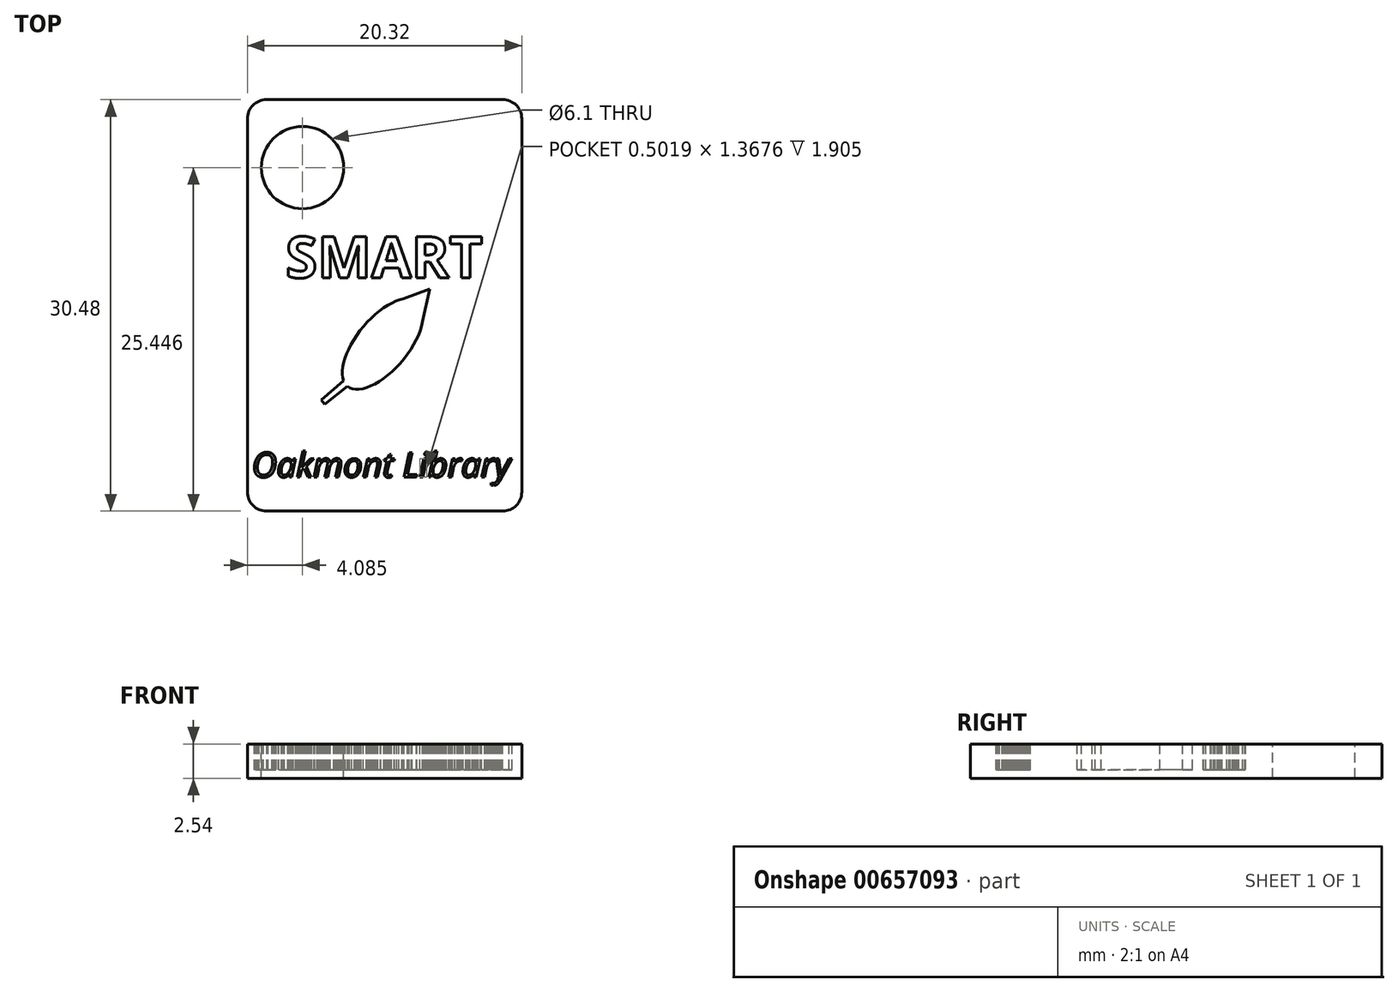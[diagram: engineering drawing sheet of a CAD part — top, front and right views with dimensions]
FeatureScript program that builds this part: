
annotation { "Feature Type Name" : "Feature", "Feature Type Description" : "" }
export const myFeature = defineFeature(function(context is Context, id is Id, definition is map)
    precondition{}
    {
        {
            var Q0;
            Q0=qCreatedBy(makeId("Top.planeOp"),FACE);
            var sketch = newSketch(context, id + "F0", { "sketchPlane" : qUnion([Q0])});
            skLineSegment(sketch, "E0.bottom", {"start": v(10.16, -15.24) * mm, "end": v(-10.16, -15.24) * mm});
            skLineSegment(sketch, "E0.top", {"start": v(10.16, 15.24) * mm, "end": v(-10.16, 15.24) * mm});
            skLineSegment(sketch, "E0.left", {"start": v(10.16, -15.24) * mm, "end": v(10.16, 15.24) * mm});
            skLineSegment(sketch, "E0.right", {"start": v(-10.16, -15.24) * mm, "end": v(-10.16, 15.24) * mm});
            skPoint(sketch, "E0.middle", {"position": v(0, 0) * mm});
            skSolve(sketch);
        }
        {
            var Q0;
            Q0 = qSketchRegion(id + "F0", true);
            extrude(context, id + "F1", {"entities" : qUnion([Q0]), "depth" : 2.54 * mm, "offsetDistance" : 25.4 * mm});
        }
        {
            var Q0;
            Q0=makeQuery(id+"F1.opExtrude","CAP_FACE",FACE,{"disambiguationData":[OSD([sQuery(id+"F0.wireOp",EDGE,"E0.bottom"),sQuery(id+"F0.wireOp",EDGE,"E0.top"),sQuery(id+"F0.wireOp",EDGE,"E0.left"),sQuery(id+"F0.wireOp",EDGE,"E0.right")])],"isStart":false});
            var sketch = newSketch(context, id + "F2", { "sketchPlane" : qUnion([Q0])});
            skText(sketch, "E1", { "text": "SMART\n", "fontName": "OpenSans-Bold.ttf"});
            const initialGuessF2  = {"E1": [-0.00734, 0.00204, 1, 0, 0.00307]};
            skSetInitialGuess(sketch, initialGuessF2);
            skSolve(sketch);
        }
        {
            var Q0;
            Q0 = qSketchRegion(id + "F2", true);
            extrude(context, id + "F3", {"entities" : qUnion([Q0]), "operationType" : NewBodyOperationType.REMOVE, "oppositeDirection" : true, "depth" : 1.9 * mm, "offsetDistance" : 25.4 * mm});
        }
        {
            var Q0;
            Q0=makeQuery(id+"F1.opExtrude","SWEPT_EDGE",EDGE,{"disambiguationData":[OSD([sQuery(id+"F0.wireOp",EDGE,"E0.top"),sQuery(id+"F0.wireOp",EDGE,"E0.right")])]});
            var Q1;
            Q1=makeQuery(id+"F1.opExtrude","SWEPT_EDGE",EDGE,{"disambiguationData":[OSD([sQuery(id+"F0.wireOp",EDGE,"E0.top"),sQuery(id+"F0.wireOp",EDGE,"E0.left")])]});
            var Q2;
            Q2=makeQuery(id+"F1.opExtrude","SWEPT_EDGE",EDGE,{"disambiguationData":[OSD([sQuery(id+"F0.wireOp",EDGE,"E0.bottom"),sQuery(id+"F0.wireOp",EDGE,"E0.left")])]});
            var Q3;
            Q3=makeQuery(id+"F1.opExtrude","SWEPT_EDGE",EDGE,{"disambiguationData":[OSD([sQuery(id+"F0.wireOp",EDGE,"E0.bottom"),sQuery(id+"F0.wireOp",EDGE,"E0.right")])]});
            fillet(context, id + "F4", {"entities" : qUnion([Q0, Q1, Q2, Q3]), "radius" : 1.41 * mm, "tangentPropagation" : true, "allowEdgeOverflow" : false});
        }
        {
            var Q0;
            {var subQ0=sQuery(id+"F0.wireOp",EDGE,"E0.left");var subQ1=sQuery(id+"F0.wireOp",EDGE,"E0.bottom");var subQ2=sQuery(id+"F0.wireOp",EDGE,"E0.right");var subQ3=sQuery(id+"F0.wireOp",EDGE,"E0.top");Q0=makeQuery(id+"F3.boolean.opBoolean","SPLIT",FACE,{"disambiguationData":[TD([makeQuery(id+"F1.opExtrude","SWEPT_FACE",FACE,{"disambiguationData":[OSD([subQ1])]})])],"derivedFrom":makeQuery(id+"F1.opExtrude","CAP_FACE",FACE,{"disambiguationData":[OSD([subQ1,subQ3,subQ0,subQ2])],"isStart":false})});}
            var sketch = newSketch(context, id + "F5", { "sketchPlane" : qUnion([Q0])});
            skText(sketch, "E2", { "text": "Oakmont Library\n", "fontName": "OpenSans-Italic.ttf"});
            const initialGuessF5  = {"E2": [-0.00983, -0.01273, 1, 0, 0.00184]};
            skSetInitialGuess(sketch, initialGuessF5);
            skSolve(sketch);
        }
        {
            var Q0;
            Q0 = qSketchRegion(id + "F5", true);
            extrude(context, id + "F6", {"entities" : qUnion([Q0]), "operationType" : NewBodyOperationType.REMOVE, "oppositeDirection" : true, "depth" : 1.9 * mm, "offsetDistance" : 25.4 * mm});
        }
        {
            var Q0;
            {var subQ37=sQuery(id+"F0.wireOp",EDGE,"E0.bottom");var subQ38=makeQuery(id+"F1.opExtrude","SWEPT_FACE",FACE,{"disambiguationData":[OSD([subQ37])]});var subQ43=sQuery(id+"F0.wireOp",EDGE,"E0.right");var subQ47=sQuery(id+"F0.wireOp",EDGE,"E0.top");var subQ51=sQuery(id+"F0.wireOp",EDGE,"E0.left");Q0=makeQuery(id+"F6.boolean.opBoolean","SPLIT",FACE,{"disambiguationData":[TD([subQ38])],"derivedFrom":makeQuery(id+"F3.boolean.opBoolean","SPLIT",FACE,{"disambiguationData":[TD([subQ38])],"derivedFrom":makeQuery(id+"F1.opExtrude","CAP_FACE",FACE,{"disambiguationData":[OSD([subQ37,subQ47,subQ51,subQ43])],"isStart":false})})});}
            var sketch = newSketch(context, id + "F7", { "sketchPlane" : qUnion([Q0])});
            skCircle(sketch, "E3", {"center": v(-6.07, 10.2) * mm, "radius": 3.05 * mm});
            skSolve(sketch);
        }
        {
            var Q0;
            Q0 = qSketchRegion(id + "F7", true);
            extrude(context, id + "F8", {"entities" : qUnion([Q0]), "operationType" : NewBodyOperationType.REMOVE, "oppositeDirection" : true, "depth" : 25.4 * mm, "offsetDistance" : 25.4 * mm});
        }
        {
            var Q0;
            {var subQ10=sQuery(id+"F0.wireOp",EDGE,"E0.top");var subQ15=sQuery(id+"F0.wireOp",EDGE,"E0.bottom");var subQ16=makeQuery(id+"F1.opExtrude","SWEPT_FACE",FACE,{"disambiguationData":[OSD([subQ15])]});var subQ64=sQuery(id+"F0.wireOp",EDGE,"E0.right");var subQ67=sQuery(id+"F0.wireOp",EDGE,"E0.left");Q0=makeQuery(id+"F6.boolean.opBoolean","SPLIT",FACE,{"disambiguationData":[TD([subQ16])],"derivedFrom":makeQuery(id+"F3.boolean.opBoolean","SPLIT",FACE,{"disambiguationData":[TD([subQ16])],"derivedFrom":makeQuery(id+"F1.opExtrude","CAP_FACE",FACE,{"disambiguationData":[OSD([subQ15,subQ10,subQ67,subQ64])],"isStart":false})})});}
            var sketch = newSketch(context, id + "F9", { "sketchPlane" : qUnion([Q0])});
            skEllipse(sketch, "E4", {"center": v(-0.14, -2.85) * mm, "majorRadius": 4.08 * mm, "minorRadius": 1.92 * mm, "majorAxis": v(-0.64, -0.77)});
            skLineSegment(sketch, "E5", {"start": v(-3.04, -5.57) * mm, "end": v(-4.7, -7) * mm});
            skLineSegment(sketch, "E6", {"start": v(-4.7, -7) * mm, "end": v(-4.44, -7.34) * mm});
            skLineSegment(sketch, "E7", {"start": v(-4.44, -7.34) * mm, "end": v(-2.74, -6) * mm});
            skLineSegment(sketch, "E8", {"start": v(1.4, 0.49) * mm, "end": v(3.35, 1.21) * mm});
            skLineSegment(sketch, "E9", {"start": v(3.35, 1.21) * mm, "end": v(2.75, -1.51) * mm});
            skSolve(sketch);
        }
        {
            var Q0;
            Q0 = qSketchRegion(id + "F9", true);
            extrude(context, id + "F10", {"entities" : qUnion([Q0]), "operationType" : NewBodyOperationType.REMOVE, "oppositeDirection" : true, "depth" : 1.9 * mm, "offsetDistance" : 25.4 * mm});
        }
    });
